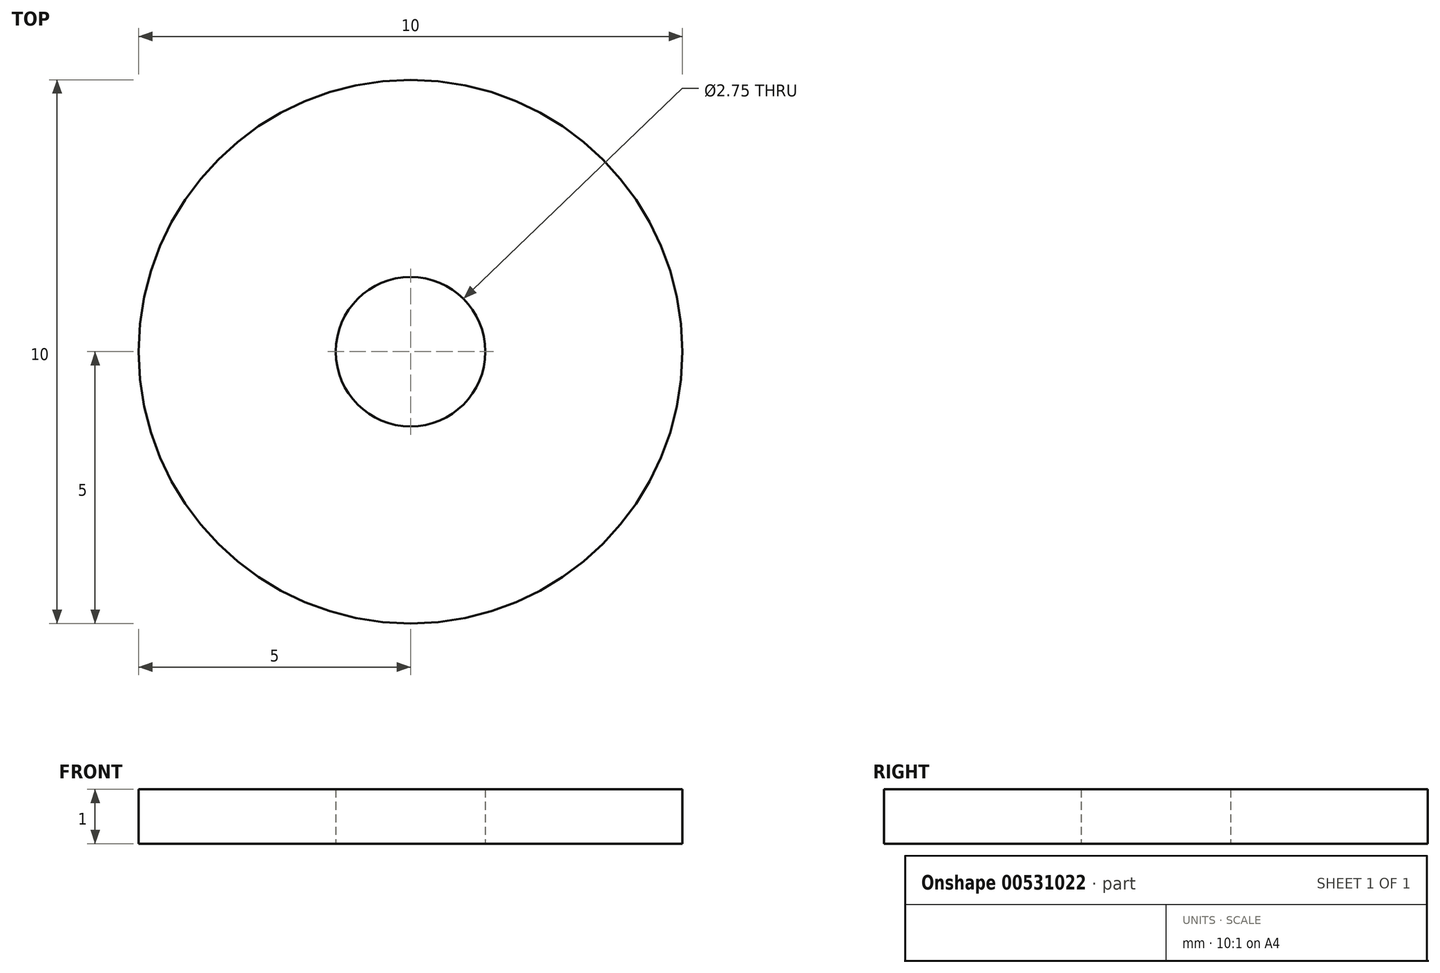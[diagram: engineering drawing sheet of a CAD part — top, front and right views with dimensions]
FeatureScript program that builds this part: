
annotation { "Feature Type Name" : "Feature", "Feature Type Description" : "" }
export const myFeature = defineFeature(function(context is Context, id is Id, definition is map)
    precondition{}
    {
        {
            var Q0;
            Q0=qCreatedBy(makeId("Top.planeOp"),FACE);
            var sketch = newSketch(context, id + "F0", { "sketchPlane" : qUnion([Q0])});
            skCircle(sketch, "E0", {"center": v(0, 0) * mm, "radius": 5 * mm});
            skCircle(sketch, "E1", {"center": v(0, 0) * mm, "radius": 1.38 * mm});
            skSolve(sketch);
        }
        {
            var Q0;
            Q0 = qSketchRegion(id + "F0", true);
            extrude(context, id + "F1", {"entities" : qUnion([Q0]), "depth" : 1 * mm, "offsetDistance" : 25 * mm});
        }
    });
